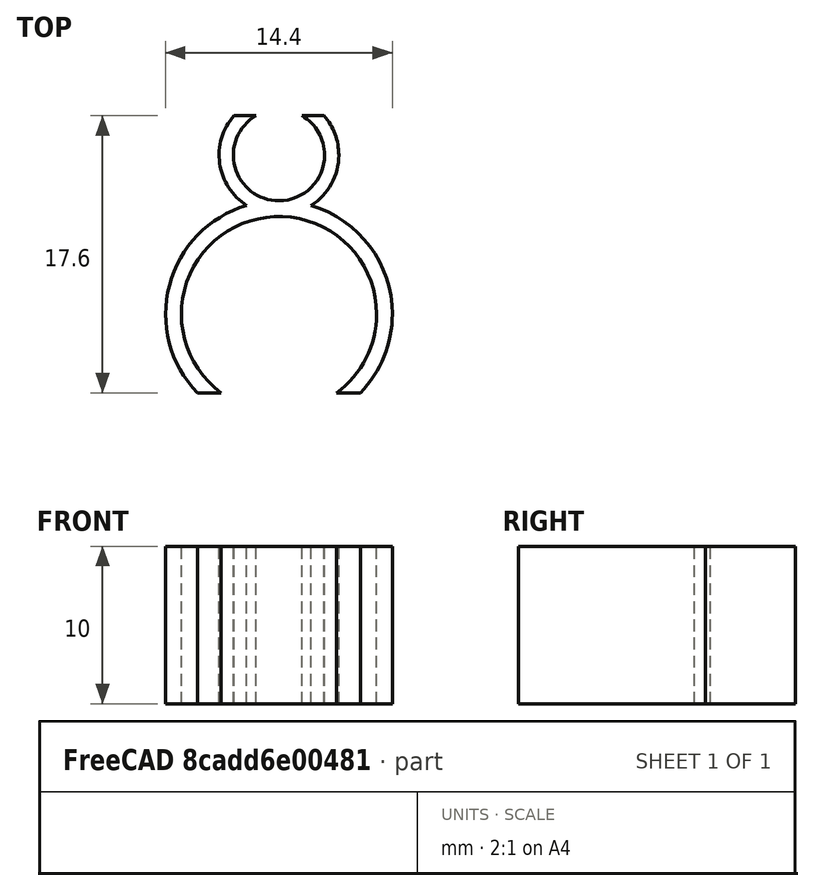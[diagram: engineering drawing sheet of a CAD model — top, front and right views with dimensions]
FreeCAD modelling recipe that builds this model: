
FCSTD DOCUMENT  (FreeCAD 0.20R29603 (Git))
Label: solder_suctiontube_holder
License: All rights reserved
LicenseURL: http://en.wikipedia.org/wiki/All_rights_reserved
objects: Part::FeaturePython×2, Part::Box×2, Part::Cut×2, Part::MultiFuse×1
note: 7 computed .brp shape members not serialized (recipe doc carries the construction recipe); baked Part::Feature solids carry a one-line shape summary decoded from their .brp

FEATURE [Part::FeaturePython] Tube  # WARN: FeaturePython — macro-defined, semantics opaque (R4)
  AttacherType = Attacher::AttachEngine3D
  Height = 10
  InnerRadius = 2.9
  OuterRadius = 3.8
  Placement = pos=(0,10.1,0) rot=(0,0,1;0rad)
FEATURE [Part::FeaturePython] Tube001  # WARN: FeaturePython — macro-defined, semantics opaque (R4)
  AttacherType = Attacher::AttachEngine3D
  Height = 10
  InnerRadius = 6.2
  OuterRadius = 7.2
FEATURE [Part::Box] Box  label="Cube"
  AttacherType = Attacher::AttachEngine3D
  Height = 10
  Length = 10
  Placement = pos=(-5,12.6,0) rot=(0,0,1;0rad)
  Width = 10
FEATURE [Part::Cut] Cut
  Base = -> Tube
  Tool = -> Box
FEATURE [Part::Box] Box001  label="Cube001"
  AttacherType = Attacher::AttachEngine3D
  Height = 10
  Length = 20
  Placement = pos=(-10,-15,0) rot=(0,0,1;0rad)
  Width = 10
FEATURE [Part::Cut] Cut001
  Base = -> Tube001
  Tool = -> Box001
FEATURE [Part::MultiFuse] Fusion
  Shapes = -> [Cut,Cut001]
